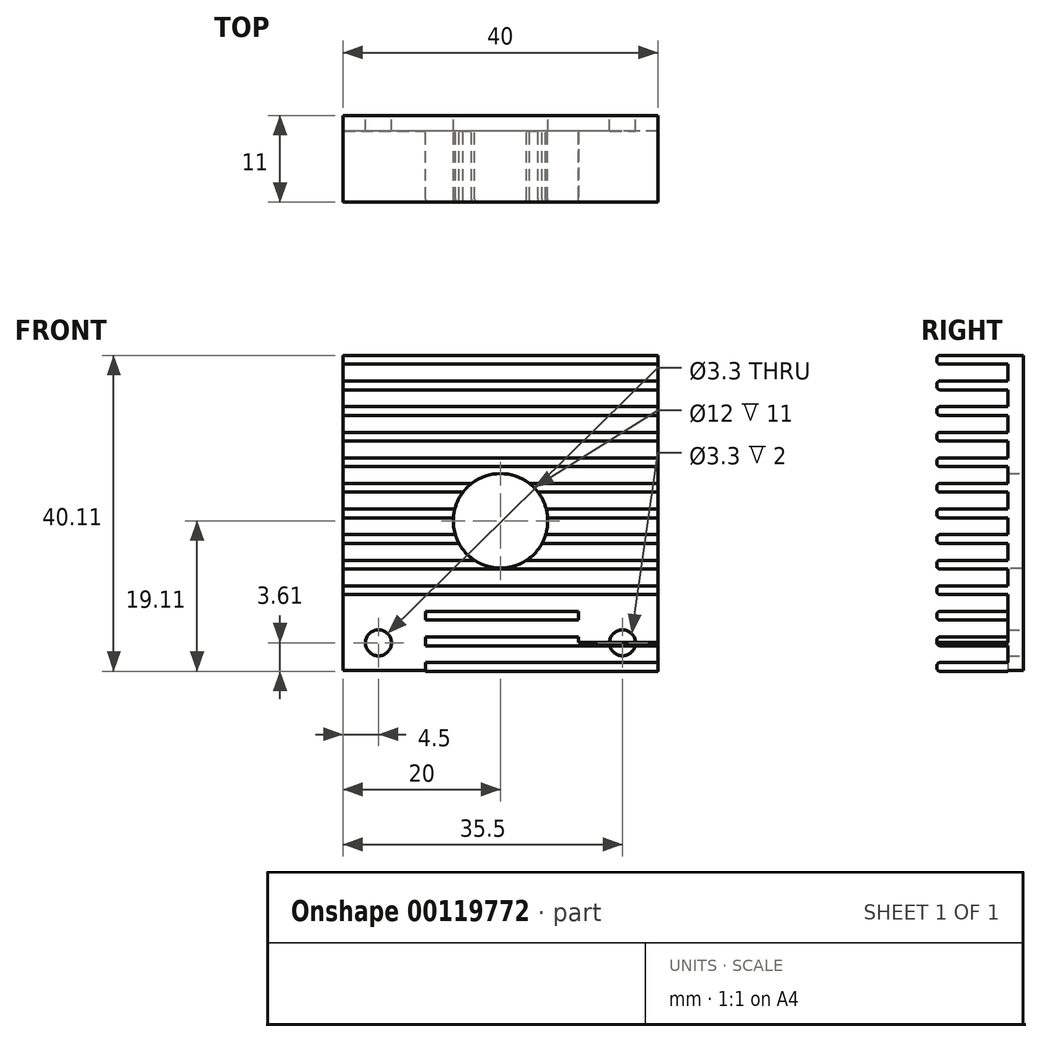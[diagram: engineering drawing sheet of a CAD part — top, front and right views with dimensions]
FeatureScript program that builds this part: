
annotation { "Feature Type Name" : "Feature", "Feature Type Description" : "" }
export const myFeature = defineFeature(function(context is Context, id is Id, definition is map)
    precondition{}
    {
        {
            var Q0;
            Q0=qCreatedBy(makeId("Top.planeOp"),FACE);
            var sketch = newSketch(context, id + "F0", { "sketchPlane" : qUnion([Q0])});
            skLineSegment(sketch, "E0", {"start": v(0, 20) * mm, "end": v(0, -20) * mm, "construction": true});
            skLineSegment(sketch, "E1", {"start": v(20, 20) * mm, "end": v(20, -20) * mm});
            skLineSegment(sketch, "E2", {"start": v(-20, 20) * mm, "end": v(-20, -20) * mm});
            skLineSegment(sketch, "E3", {"start": v(-20, 0) * mm, "end": v(20, 0) * mm, "construction": true});
            skLineSegment(sketch, "E4", {"start": v(-20, 20) * mm, "end": v(20, 20) * mm});
            skLineSegment(sketch, "E5", {"start": v(-20, -20) * mm, "end": v(20, -20) * mm});
            skPoint(sketch, "E6.orphan", {"position": v(-43.73, 20) * mm});
            skPoint(sketch, "E7.orphan", {"position": v(-42.9, 0) * mm});
            skPoint(sketch, "E8.orphan", {"position": v(-42.07, -20) * mm});
            skPoint(sketch, "E9.orphan", {"position": v(20, 28.35) * mm});
            skPoint(sketch, "E10.orphan", {"position": v(0, 28.12) * mm});
            skPoint(sketch, "E11.orphan", {"position": v(-20, 28.93) * mm});
            skLineSegment(sketch, "E12", {"start": v(-26.22, -16.5) * mm, "end": v(31.97, -16.5) * mm, "construction": true});
            skLineSegment(sketch, "E13", {"start": v(15.5, -23.6) * mm, "end": v(15.5, 22.14) * mm, "construction": true});
            skLineSegment(sketch, "E14", {"start": v(-15.5, 22.27) * mm, "end": v(-15.5, -32.23) * mm, "construction": true});
            skCircle(sketch, "E15", {"center": v(-15.5, -16.5) * mm, "radius": 1.65 * mm});
            skCircle(sketch, "E16", {"center": v(15.5, -16.5) * mm, "radius": 1.65 * mm});
            skLineSegment(sketch, "E17", {"start": v(9.9, 22.51) * mm, "end": v(9.9, -37.4) * mm, "construction": true});
            skLineSegment(sketch, "E18", {"start": v(-9.5, 22.14) * mm, "end": v(-9.5, -26.68) * mm, "construction": true});
            skLineSegment(sketch, "E19", {"start": v(-28.44, -10.5) * mm, "end": v(54.9, -10.5) * mm, "construction": true});
            skLineSegment(sketch, "E20", {"start": v(9.9, -10.5) * mm, "end": v(9.9, -20) * mm});
            skLineSegment(sketch, "E21", {"start": v(9.9, -10.5) * mm, "end": v(20, -10.5) * mm});
            skLineSegment(sketch, "E22", {"start": v(-20, -10.5) * mm, "end": v(-9.5, -10.5) * mm});
            skLineSegment(sketch, "E23", {"start": v(-9.5, -10.5) * mm, "end": v(-9.5, -20) * mm});
            skPoint(sketch, "E24", {"position": v(0, -1) * mm});
            skCircle(sketch, "E25", {"center": v(0, -1) * mm, "radius": 6 * mm});
            skSolve(sketch);
        }
        {
            var Q0;
            {var subQ4=sQuery(id+"F0.wireOp",EDGE,"E4");Q0=makeQuery(id+"F0.imprint","IMPRINT",FACE,{"disambiguationData":[TD([[makeQuery(id+"F0.imprint","IMPRINT",EDGE,{"derivedFrom":subQ4}),-1.0]])]});}
            var Q1;
            Q1=makeQuery(id+"F0.imprint","IMPRINT",FACE,{"disambiguationData":[TD([[makeQuery(id+"F0.imprint","IMPRINT",EDGE,{"derivedFrom":sQuery(id+"F0.wireOp",EDGE,"E15")}),-1.0]])]});
            var Q2;
            Q2=makeQuery(id+"F0.imprint","IMPRINT",FACE,{"disambiguationData":[TD([[makeQuery(id+"F0.imprint","IMPRINT",EDGE,{"derivedFrom":sQuery(id+"F0.wireOp",EDGE,"E16")}),-1.0]])]});
            extrude(context, id + "F1", {"entities" : qUnion([Q0, Q1, Q2]), "depth" : 2 * mm, "offsetDistance" : 25 * mm});
        }
        {
            var Q0;
            Q0=qCreatedBy(makeId("Right.planeOp"),FACE);
            var sketch = newSketch(context, id + "F2", { "sketchPlane" : qUnion([Q0])});
            skLineSegment(sketch, "E26.0", {"start": v(20, 2) * mm, "end": v(-20, 2) * mm});
            skLineSegment(sketch, "E26.1", {"start": v(20, 2) * mm, "end": v(20, 0) * mm});
            skLineSegment(sketch, "E26.2", {"start": v(-20, 2) * mm, "end": v(-20, 0) * mm});
            skLineSegment(sketch, "E27", {"start": v(20, 2) * mm, "end": v(20, 11) * mm});
            skLineSegment(sketch, "E28", {"start": v(20, 11) * mm, "end": v(18.9, 11) * mm});
            skLineSegment(sketch, "E29", {"start": v(18.9, 11) * mm, "end": v(18.9, 2) * mm});
            skLineSegment(sketch, "E30", {"start": v(20, 2) * mm, "end": v(18.9, 2) * mm});
            skLineSegment(sketch, "E31.1.0.0", {"start": v(16.75, 2) * mm, "end": v(16.75, 11) * mm});
            skLineSegment(sketch, "E31.1.0.1", {"start": v(16.75, 11) * mm, "end": v(15.65, 11) * mm});
            skLineSegment(sketch, "E31.1.0.2", {"start": v(15.65, 11) * mm, "end": v(15.65, 2) * mm});
            skLineSegment(sketch, "E31.1.0.3", {"start": v(16.75, 2) * mm, "end": v(15.65, 2) * mm});
            skLineSegment(sketch, "E31.2.0.0", {"start": v(13.5, 2) * mm, "end": v(13.5, 11) * mm});
            skLineSegment(sketch, "E31.2.0.1", {"start": v(13.5, 11) * mm, "end": v(12.4, 11) * mm});
            skLineSegment(sketch, "E31.2.0.2", {"start": v(12.4, 11) * mm, "end": v(12.4, 2) * mm});
            skLineSegment(sketch, "E31.2.0.3", {"start": v(13.5, 2) * mm, "end": v(12.4, 2) * mm});
            skLineSegment(sketch, "E31.3.0.0", {"start": v(10.25, 2) * mm, "end": v(10.25, 11) * mm});
            skLineSegment(sketch, "E31.3.0.1", {"start": v(10.25, 11) * mm, "end": v(9.15, 11) * mm});
            skLineSegment(sketch, "E31.3.0.2", {"start": v(9.15, 11) * mm, "end": v(9.15, 2) * mm});
            skLineSegment(sketch, "E31.3.0.3", {"start": v(10.25, 2) * mm, "end": v(9.15, 2) * mm});
            skLineSegment(sketch, "E31.4.0.0", {"start": v(7, 2) * mm, "end": v(7, 11) * mm});
            skLineSegment(sketch, "E31.4.0.1", {"start": v(7, 11) * mm, "end": v(5.9, 11) * mm});
            skLineSegment(sketch, "E31.4.0.2", {"start": v(5.9, 11) * mm, "end": v(5.9, 2) * mm});
            skLineSegment(sketch, "E31.4.0.3", {"start": v(7, 2) * mm, "end": v(5.9, 2) * mm});
            skLineSegment(sketch, "E31.5.0.0", {"start": v(3.74, 2) * mm, "end": v(3.74, 11) * mm});
            skLineSegment(sketch, "E31.5.0.1", {"start": v(3.74, 11) * mm, "end": v(2.64, 11) * mm});
            skLineSegment(sketch, "E31.5.0.2", {"start": v(2.64, 11) * mm, "end": v(2.64, 2) * mm});
            skLineSegment(sketch, "E31.5.0.3", {"start": v(3.74, 2) * mm, "end": v(2.64, 2) * mm});
            skLineSegment(sketch, "E31.6.0.0", {"start": v(0.5, 2) * mm, "end": v(0.5, 11) * mm});
            skLineSegment(sketch, "E31.6.0.1", {"start": v(0.5, 11) * mm, "end": v(-0.6, 11) * mm});
            skLineSegment(sketch, "E31.6.0.2", {"start": v(-0.6, 11) * mm, "end": v(-0.6, 2) * mm});
            skLineSegment(sketch, "E31.6.0.3", {"start": v(0.5, 2) * mm, "end": v(-0.6, 2) * mm});
            skLineSegment(sketch, "E31.7.0.0", {"start": v(-2.76, 2) * mm, "end": v(-2.76, 11) * mm});
            skLineSegment(sketch, "E31.7.0.1", {"start": v(-2.76, 11) * mm, "end": v(-3.86, 11) * mm});
            skLineSegment(sketch, "E31.7.0.2", {"start": v(-3.86, 11) * mm, "end": v(-3.86, 2) * mm});
            skLineSegment(sketch, "E31.7.0.3", {"start": v(-2.76, 2) * mm, "end": v(-3.86, 2) * mm});
            skLineSegment(sketch, "E31.8.0.0", {"start": v(-6, 2) * mm, "end": v(-6, 11) * mm});
            skLineSegment(sketch, "E31.8.0.1", {"start": v(-6, 11) * mm, "end": v(-7.1, 11) * mm});
            skLineSegment(sketch, "E31.8.0.2", {"start": v(-7.1, 11) * mm, "end": v(-7.1, 2) * mm});
            skLineSegment(sketch, "E31.8.0.3", {"start": v(-6, 2) * mm, "end": v(-7.1, 2) * mm});
            skLineSegment(sketch, "E31.9.0.0", {"start": v(-9.26, 2) * mm, "end": v(-9.26, 11) * mm});
            skLineSegment(sketch, "E31.9.0.1", {"start": v(-9.26, 11) * mm, "end": v(-10.36, 11) * mm});
            skLineSegment(sketch, "E31.9.0.2", {"start": v(-10.36, 11) * mm, "end": v(-10.36, 2) * mm});
            skLineSegment(sketch, "E31.9.0.3", {"start": v(-9.26, 2) * mm, "end": v(-10.36, 2) * mm});
            skLineSegment(sketch, "E31.10.0.0", {"start": v(-12.51, 2) * mm, "end": v(-12.51, 11) * mm});
            skLineSegment(sketch, "E31.10.0.1", {"start": v(-12.51, 11) * mm, "end": v(-13.61, 11) * mm});
            skLineSegment(sketch, "E31.10.0.2", {"start": v(-13.61, 11) * mm, "end": v(-13.61, 2) * mm});
            skLineSegment(sketch, "E31.10.0.3", {"start": v(-12.51, 2) * mm, "end": v(-13.61, 2) * mm});
            skLineSegment(sketch, "E31.11.0.0", {"start": v(-15.76, 2) * mm, "end": v(-15.76, 11) * mm});
            skLineSegment(sketch, "E31.11.0.1", {"start": v(-15.76, 11) * mm, "end": v(-16.86, 11) * mm});
            skLineSegment(sketch, "E31.11.0.2", {"start": v(-16.86, 11) * mm, "end": v(-16.86, 2) * mm});
            skLineSegment(sketch, "E31.11.0.3", {"start": v(-15.76, 2) * mm, "end": v(-16.86, 2) * mm});
            skLineSegment(sketch, "E31.12.0.0", {"start": v(-19.01, 2) * mm, "end": v(-19.01, 11) * mm});
            skLineSegment(sketch, "E31.12.0.1", {"start": v(-19.01, 11) * mm, "end": v(-20.11, 11) * mm});
            skLineSegment(sketch, "E31.12.0.2", {"start": v(-20.11, 11) * mm, "end": v(-20.11, 2) * mm});
            skLineSegment(sketch, "E31.12.0.3", {"start": v(-19.01, 2) * mm, "end": v(-20.11, 2) * mm});
            skLineSegment(sketch, "E31.direction1", {"start": v(20, 2) * mm, "end": v(16.75, 2) * mm, "construction": true});
            skSolve(sketch);
        }
        {
            var Q0;
            Q0=makeQuery(id+"F2.imprint","IMPRINT",FACE,{"disambiguationData":[TD([[makeQuery(id+"F2.imprint","IMPRINT",EDGE,{"derivedFrom":sQuery(id+"F2.wireOp",EDGE,"E27")}),1.0]])]});
            var Q1;
            Q1=makeQuery(id+"F2.imprint","IMPRINT",FACE,{"disambiguationData":[TD([[makeQuery(id+"F2.imprint","IMPRINT",EDGE,{"derivedFrom":sQuery(id+"F2.wireOp",EDGE,"E31.1.0.0")}),1.0]])]});
            var Q2;
            Q2=makeQuery(id+"F2.imprint","IMPRINT",FACE,{"disambiguationData":[TD([[makeQuery(id+"F2.imprint","IMPRINT",EDGE,{"derivedFrom":sQuery(id+"F2.wireOp",EDGE,"E31.2.0.0")}),1.0]])]});
            var Q3;
            Q3=makeQuery(id+"F2.imprint","IMPRINT",FACE,{"disambiguationData":[TD([[makeQuery(id+"F2.imprint","IMPRINT",EDGE,{"derivedFrom":sQuery(id+"F2.wireOp",EDGE,"E31.3.0.0")}),1.0]])]});
            var Q4;
            Q4=makeQuery(id+"F2.imprint","IMPRINT",FACE,{"disambiguationData":[TD([[makeQuery(id+"F2.imprint","IMPRINT",EDGE,{"derivedFrom":sQuery(id+"F2.wireOp",EDGE,"E31.4.0.0")}),1.0]])]});
            var Q5;
            Q5=makeQuery(id+"F2.imprint","IMPRINT",FACE,{"disambiguationData":[TD([[makeQuery(id+"F2.imprint","IMPRINT",EDGE,{"derivedFrom":sQuery(id+"F2.wireOp",EDGE,"E31.5.0.0")}),1.0]])]});
            var Q6;
            Q6=makeQuery(id+"F2.imprint","IMPRINT",FACE,{"disambiguationData":[TD([[makeQuery(id+"F2.imprint","IMPRINT",EDGE,{"derivedFrom":sQuery(id+"F2.wireOp",EDGE,"E31.6.0.0")}),1.0]])]});
            var Q7;
            Q7=makeQuery(id+"F2.imprint","IMPRINT",FACE,{"disambiguationData":[TD([[makeQuery(id+"F2.imprint","IMPRINT",EDGE,{"derivedFrom":sQuery(id+"F2.wireOp",EDGE,"E31.7.0.0")}),1.0]])]});
            var Q8;
            Q8=makeQuery(id+"F2.imprint","IMPRINT",FACE,{"disambiguationData":[TD([[makeQuery(id+"F2.imprint","IMPRINT",EDGE,{"derivedFrom":sQuery(id+"F2.wireOp",EDGE,"E31.9.0.0")}),1.0]])]});
            var Q9;
            Q9=makeQuery(id+"F2.imprint","IMPRINT",FACE,{"disambiguationData":[TD([[makeQuery(id+"F2.imprint","IMPRINT",EDGE,{"derivedFrom":sQuery(id+"F2.wireOp",EDGE,"E31.10.0.0")}),1.0]])]});
            var Q10;
            Q10=makeQuery(id+"F2.imprint","IMPRINT",FACE,{"disambiguationData":[TD([[makeQuery(id+"F2.imprint","IMPRINT",EDGE,{"derivedFrom":sQuery(id+"F2.wireOp",EDGE,"E31.11.0.0")}),1.0]])]});
            var Q11;
            Q11=makeQuery(id+"F2.imprint","IMPRINT",FACE,{"disambiguationData":[TD([[makeQuery(id+"F2.imprint","IMPRINT",EDGE,{"derivedFrom":sQuery(id+"F2.wireOp",EDGE,"E31.12.0.0")}),1.0]])]});
            var Q12;
            Q12=makeQuery(id+"F2.imprint","IMPRINT",FACE,{"disambiguationData":[TD([[makeQuery(id+"F2.imprint","IMPRINT",EDGE,{"derivedFrom":sQuery(id+"F2.wireOp",EDGE,"E31.8.0.0")}),1.0]])]});
            extrude(context, id + "F3", {"entities" : qUnion([Q0, Q1, Q2, Q3, Q4, Q5, Q6, Q7, Q8, Q9, Q10, Q11, Q12]), "operationType" : NewBodyOperationType.ADD, "depth" : 40 * mm, "offsetDistance" : 25 * mm, "symmetric" : true});
        }
        {
            var Q0;
            Q0=makeQuery(id+"F0.imprint","IMPRINT",FACE,{"disambiguationData":[TD([[makeQuery(id+"F0.imprint","IMPRINT",EDGE,{"derivedFrom":sQuery(id+"F0.wireOp",EDGE,"E25")}),1.0]])]});
            extrude(context, id + "F4", {"entities" : qUnion([Q0]), "operationType" : NewBodyOperationType.REMOVE, "depth" : 19 * mm, "offsetDistance" : 25 * mm});
        }
        {
            var Q0;
            Q0=makeQuery(id+"F3.opExtrude","SWEPT_EDGE",EDGE,{"disambiguationData":[OSD([sQuery(id+"F2.wireOp",EDGE,"E27"),sQuery(id+"F2.wireOp",EDGE,"E28")])]});
            var Q1;
            Q1=makeQuery(id+"F3.opExtrude","SWEPT_EDGE",EDGE,{"disambiguationData":[OSD([sQuery(id+"F2.wireOp",EDGE,"E28"),sQuery(id+"F2.wireOp",EDGE,"E29")])]});
            var Q2;
            Q2=makeQuery(id+"F3.opExtrude","SWEPT_EDGE",EDGE,{"disambiguationData":[OSD([sQuery(id+"F2.wireOp",EDGE,"E31.1.0.0"),sQuery(id+"F2.wireOp",EDGE,"E31.1.0.1")])]});
            var Q3;
            Q3=makeQuery(id+"F3.opExtrude","SWEPT_EDGE",EDGE,{"disambiguationData":[OSD([sQuery(id+"F2.wireOp",EDGE,"E31.1.0.1"),sQuery(id+"F2.wireOp",EDGE,"E31.1.0.2")])]});
            var Q4;
            Q4=makeQuery(id+"F3.opExtrude","SWEPT_EDGE",EDGE,{"disambiguationData":[OSD([sQuery(id+"F2.wireOp",EDGE,"E31.2.0.0"),sQuery(id+"F2.wireOp",EDGE,"E31.2.0.1")])]});
            var Q5;
            Q5=makeQuery(id+"F3.opExtrude","SWEPT_EDGE",EDGE,{"disambiguationData":[OSD([sQuery(id+"F2.wireOp",EDGE,"E31.2.0.1"),sQuery(id+"F2.wireOp",EDGE,"E31.2.0.2")])]});
            var Q6;
            Q6=makeQuery(id+"F3.opExtrude","SWEPT_EDGE",EDGE,{"disambiguationData":[OSD([sQuery(id+"F2.wireOp",EDGE,"E31.3.0.0"),sQuery(id+"F2.wireOp",EDGE,"E31.3.0.1")])]});
            var Q7;
            Q7=makeQuery(id+"F3.opExtrude","SWEPT_EDGE",EDGE,{"disambiguationData":[OSD([sQuery(id+"F2.wireOp",EDGE,"E31.3.0.1"),sQuery(id+"F2.wireOp",EDGE,"E31.3.0.2")])]});
            var Q8;
            Q8=makeQuery(id+"F3.opExtrude","SWEPT_EDGE",EDGE,{"disambiguationData":[OSD([sQuery(id+"F2.wireOp",EDGE,"E31.4.0.0"),sQuery(id+"F2.wireOp",EDGE,"E31.4.0.1")])]});
            var Q9;
            Q9=makeQuery(id+"F3.opExtrude","SWEPT_EDGE",EDGE,{"disambiguationData":[OSD([sQuery(id+"F2.wireOp",EDGE,"E31.4.0.1"),sQuery(id+"F2.wireOp",EDGE,"E31.4.0.2")])]});
            var Q10;
            Q10=makeQuery(id+"F3.opExtrude","SWEPT_EDGE",EDGE,{"disambiguationData":[OSD([sQuery(id+"F2.wireOp",EDGE,"E31.5.0.0"),sQuery(id+"F2.wireOp",EDGE,"E31.5.0.1")])]});
            var Q11;
            Q11=makeQuery(id+"F3.opExtrude","SWEPT_EDGE",EDGE,{"disambiguationData":[OSD([sQuery(id+"F2.wireOp",EDGE,"E31.5.0.1"),sQuery(id+"F2.wireOp",EDGE,"E31.5.0.2")])]});
            var Q12;
            Q12=makeQuery(id+"F3.opExtrude","SWEPT_EDGE",EDGE,{"disambiguationData":[OSD([sQuery(id+"F2.wireOp",EDGE,"E31.6.0.0"),sQuery(id+"F2.wireOp",EDGE,"E31.6.0.1")])]});
            var Q13;
            Q13=makeQuery(id+"F3.opExtrude","SWEPT_EDGE",EDGE,{"disambiguationData":[OSD([sQuery(id+"F2.wireOp",EDGE,"E31.6.0.1"),sQuery(id+"F2.wireOp",EDGE,"E31.6.0.2")])]});
            var Q14;
            Q14=makeQuery(id+"F3.opExtrude","SWEPT_EDGE",EDGE,{"disambiguationData":[OSD([sQuery(id+"F2.wireOp",EDGE,"E31.7.0.0"),sQuery(id+"F2.wireOp",EDGE,"E31.7.0.1")])]});
            var Q15;
            Q15=makeQuery(id+"F3.opExtrude","SWEPT_EDGE",EDGE,{"disambiguationData":[OSD([sQuery(id+"F2.wireOp",EDGE,"E31.7.0.1"),sQuery(id+"F2.wireOp",EDGE,"E31.7.0.2")])]});
            var Q16;
            Q16=makeQuery(id+"F3.opExtrude","SWEPT_EDGE",EDGE,{"disambiguationData":[OSD([sQuery(id+"F2.wireOp",EDGE,"E31.8.0.0"),sQuery(id+"F2.wireOp",EDGE,"E31.8.0.1")])]});
            var Q17;
            Q17=makeQuery(id+"F3.opExtrude","SWEPT_EDGE",EDGE,{"disambiguationData":[OSD([sQuery(id+"F2.wireOp",EDGE,"E31.8.0.1"),sQuery(id+"F2.wireOp",EDGE,"E31.8.0.2")])]});
            var Q18;
            Q18=makeQuery(id+"F3.opExtrude","SWEPT_EDGE",EDGE,{"disambiguationData":[OSD([sQuery(id+"F2.wireOp",EDGE,"E31.9.0.0"),sQuery(id+"F2.wireOp",EDGE,"E31.9.0.1")])]});
            var Q19;
            Q19=makeQuery(id+"F3.opExtrude","SWEPT_EDGE",EDGE,{"disambiguationData":[OSD([sQuery(id+"F2.wireOp",EDGE,"E31.9.0.1"),sQuery(id+"F2.wireOp",EDGE,"E31.9.0.2")])]});
            var Q20;
            Q20=makeQuery(id+"F4.opExtrude","SWEPT_EDGE",EDGE,{"disambiguationData":[OSD([sQuery(id+"F2.wireOp",EDGE,"E31.10.0.0"),sQuery(id+"F2.wireOp",EDGE,"E31.10.0.1")])]});
            var Q21;
            Q21=makeQuery(id+"F4.opExtrude","SWEPT_EDGE",EDGE,{"disambiguationData":[OSD([sQuery(id+"F2.wireOp",EDGE,"E31.10.0.1"),sQuery(id+"F2.wireOp",EDGE,"E31.10.0.2")])]});
            var Q22;
            Q22=makeQuery(id+"F4.opExtrude","SWEPT_EDGE",EDGE,{"disambiguationData":[OSD([sQuery(id+"F2.wireOp",EDGE,"E31.11.0.0"),sQuery(id+"F2.wireOp",EDGE,"E31.11.0.1")])]});
            var Q23;
            Q23=makeQuery(id+"F4.opExtrude","SWEPT_EDGE",EDGE,{"disambiguationData":[OSD([sQuery(id+"F2.wireOp",EDGE,"E31.11.0.1"),sQuery(id+"F2.wireOp",EDGE,"E31.11.0.2")])]});
            var Q24;
            Q24=makeQuery(id+"F4.opExtrude","SWEPT_EDGE",EDGE,{"disambiguationData":[OSD([sQuery(id+"F2.wireOp",EDGE,"E31.12.0.0"),sQuery(id+"F2.wireOp",EDGE,"E31.12.0.1")])]});
            var Q25;
            Q25=makeQuery(id+"F4.opExtrude","SWEPT_EDGE",EDGE,{"disambiguationData":[OSD([sQuery(id+"F2.wireOp",EDGE,"E31.12.0.1"),sQuery(id+"F2.wireOp",EDGE,"E31.12.0.2")])]});
            var Q26;
            Q26=makeQuery(id+"F3.opExtrude","SWEPT_EDGE",EDGE,{"disambiguationData":[OSD([sQuery(id+"F2.wireOp",EDGE,"E31.10.0.1"),sQuery(id+"F2.wireOp",EDGE,"E31.10.0.2")])]});
            var Q27;
            Q27=makeQuery(id+"F3.opExtrude","SWEPT_EDGE",EDGE,{"disambiguationData":[OSD([sQuery(id+"F2.wireOp",EDGE,"E31.10.0.0"),sQuery(id+"F2.wireOp",EDGE,"E31.10.0.1")])]});
            var Q28;
            Q28=makeQuery(id+"F3.opExtrude","SWEPT_EDGE",EDGE,{"disambiguationData":[OSD([sQuery(id+"F2.wireOp",EDGE,"E31.11.0.1"),sQuery(id+"F2.wireOp",EDGE,"E31.11.0.2")])]});
            var Q29;
            Q29=makeQuery(id+"F3.opExtrude","SWEPT_EDGE",EDGE,{"disambiguationData":[OSD([sQuery(id+"F2.wireOp",EDGE,"E31.11.0.0"),sQuery(id+"F2.wireOp",EDGE,"E31.11.0.1")])]});
            var Q30;
            Q30=makeQuery(id+"F3.opExtrude","SWEPT_EDGE",EDGE,{"disambiguationData":[OSD([sQuery(id+"F2.wireOp",EDGE,"E31.12.0.0"),sQuery(id+"F2.wireOp",EDGE,"E31.12.0.1")])]});
            var Q31;
            Q31=makeQuery(id+"F3.opExtrude","SWEPT_EDGE",EDGE,{"disambiguationData":[OSD([sQuery(id+"F2.wireOp",EDGE,"E31.12.0.1"),sQuery(id+"F2.wireOp",EDGE,"E31.12.0.2")])]});
            fillet(context, id + "F5", {"entities" : qUnion([Q0, Q1, Q2, Q3, Q4, Q5, Q6, Q7, Q8, Q9, Q10, Q11, Q12, Q13, Q14, Q15, Q16, Q17, Q18, Q19, Q20, Q21, Q22, Q23, Q24, Q25, Q26, Q27, Q28, Q29, Q30, Q31]), "radius" : 0.4 * mm, "tangentPropagation" : true, "allowEdgeOverflow" : false});
        }
        {
            var Q0;
            Q0=makeQuery(id+"F3.opExtrude","SWEPT_FACE",FACE,{"disambiguationData":[OSD([sQuery(id+"F2.wireOp",EDGE,"E31.11.0.1")])]});
            var sketch = newSketch(context, id + "F6", { "sketchPlane" : qUnion([Q0])});
            skLineSegment(sketch, "E32.0", {"start": v(-9.5, -10.5) * mm, "end": v(-9.5, -20) * mm});
            skLineSegment(sketch, "E32.1", {"start": v(-20, -10.5) * mm, "end": v(-9.5, -10.5) * mm});
            skLineSegment(sketch, "E32.2", {"start": v(9.9, -10.5) * mm, "end": v(9.9, -20) * mm});
            skLineSegment(sketch, "E32.3", {"start": v(9.9, -10.5) * mm, "end": v(20, -10.5) * mm});
            skLineSegment(sketch, "E33", {"start": v(-20, -10.5) * mm, "end": v(-20, -20) * mm});
            skLineSegment(sketch, "E34", {"start": v(-20, -20) * mm, "end": v(-9.5, -20) * mm});
            skLineSegment(sketch, "E35", {"start": v(20, -10.5) * mm, "end": v(20, -20) * mm});
            skLineSegment(sketch, "E36", {"start": v(20, -20) * mm, "end": v(9.9, -20) * mm});
            skLineSegment(sketch, "E37.trimOffspring", {"start": v(9.9, -20) * mm, "end": v(20, -20) * mm});
            skPoint(sketch, "E38.orphan", {"position": v(-20, 20) * mm});
            skLineSegment(sketch, "E39", {"start": v(-9.5, -20) * mm, "end": v(-9.5, -21.12) * mm});
            skLineSegment(sketch, "E40", {"start": v(-9.5, -21.12) * mm, "end": v(-20, -21.12) * mm});
            skLineSegment(sketch, "E41", {"start": v(-20, -21.12) * mm, "end": v(-20, -20) * mm});
            skLineSegment(sketch, "E42", {"start": v(9.9, -20) * mm, "end": v(9.9, -21.12) * mm});
            skLineSegment(sketch, "E43", {"start": v(9.9, -21.12) * mm, "end": v(20, -21.12) * mm});
            skLineSegment(sketch, "E44", {"start": v(20, -21.12) * mm, "end": v(20, -20) * mm});
            skSolve(sketch);
        }
        {
            var Q0;
            {var subQ0=sQuery(id+"F6.wireOp",EDGE,"E32.1");Q0=makeQuery(id+"F6.imprint","IMPRINT",FACE,{"disambiguationData":[TD([[makeQuery(id+"F6.imprint","IMPRINT",EDGE,{"derivedFrom":subQ0}),-1.0]])]});}
            var Q1;
            {var subQ0=sQuery(id+"F6.wireOp",EDGE,"E34");Q1=makeQuery(id+"F6.imprint","IMPRINT",FACE,{"disambiguationData":[TD([[makeQuery(id+"F6.imprint","IMPRINT",EDGE,{"derivedFrom":subQ0}),1.0]])]});}
            var Q2;
            {var subQ0=sQuery(id+"F6.wireOp",EDGE,"E32.0");var subQ1=sQuery(id+"F2.wireOp",EDGE,"E31.11.0.1");var subQ2=makeQuery(id+"F3.opExtrude","SWEPT_FACE",FACE,{"disambiguationData":[OSD([subQ1])]});var subQ3=makeQuery(id+"F5.opFillet","BLEND_EDGE",EDGE,{"blendedFrom":[makeQuery(id+"F3.opExtrude","SWEPT_EDGE",EDGE,{"disambiguationData":[OSD([sQuery(id+"F2.wireOp",EDGE,"E31.11.0.0"),subQ1])]}),subQ2],"blendedInto":[subQ2]});var subQ4=makeQuery(id+"F6.imprint","INTERSECT",VERTEX,{"derivedFrom":[subQ3,subQ0]});Q2=makeQuery(id+"F6.imprint","IMPRINT",FACE,{"disambiguationData":[TD([[makeQuery(id+"F6.imprint","IMPRINT",EDGE,{"disambiguationData":[TD([[subQ4,-1.0]])],"derivedFrom":subQ0}),-1.0]])]});}
            var Q3;
            {var subQ0=sQuery(id+"F6.wireOp",EDGE,"E32.3");Q3=makeQuery(id+"F6.imprint","IMPRINT",FACE,{"disambiguationData":[TD([[makeQuery(id+"F6.imprint","IMPRINT",EDGE,{"derivedFrom":subQ0}),-1.0]])]});}
            var Q4;
            {var subQ0=sQuery(id+"F6.wireOp",EDGE,"E32.2");var subQ1=sQuery(id+"F2.wireOp",EDGE,"E31.11.0.1");var subQ2=makeQuery(id+"F3.opExtrude","SWEPT_FACE",FACE,{"disambiguationData":[OSD([subQ1])]});var subQ3=makeQuery(id+"F5.opFillet","BLEND_EDGE",EDGE,{"blendedFrom":[makeQuery(id+"F3.opExtrude","SWEPT_EDGE",EDGE,{"disambiguationData":[OSD([sQuery(id+"F2.wireOp",EDGE,"E31.11.0.0"),subQ1])]}),subQ2],"blendedInto":[subQ2]});var subQ4=makeQuery(id+"F6.imprint","INTERSECT",VERTEX,{"derivedFrom":[subQ3,subQ0]});Q4=makeQuery(id+"F6.imprint","IMPRINT",FACE,{"disambiguationData":[TD([[makeQuery(id+"F6.imprint","IMPRINT",EDGE,{"disambiguationData":[TD([[subQ4,-1.0]])],"derivedFrom":subQ0}),1.0]])]});}
            var Q5;
            {var subQ0=sQuery(id+"F6.wireOp",EDGE,"E37.trimOffspring");Q5=makeQuery(id+"F6.imprint","IMPRINT",FACE,{"disambiguationData":[TD([[makeQuery(id+"F6.imprint","IMPRINT",EDGE,{"derivedFrom":subQ0}),1.0]])]});}
            var Q6;
            Q6=makeQuery(id+"F6.imprint","IMPRINT",FACE,{"disambiguationData":[TD([[makeQuery(id+"F6.imprint","IMPRINT",EDGE,{"derivedFrom":sQuery(id+"F6.wireOp",EDGE,"E34")}),-1.0]])]});
            var Q7;
            Q7=makeQuery(id+"F6.imprint","IMPRINT",FACE,{"disambiguationData":[TD([[makeQuery(id+"F6.imprint","IMPRINT",EDGE,{"derivedFrom":sQuery(id+"F6.wireOp",EDGE,"E37.trimOffspring")}),-1.0]])]});
            extrude(context, id + "F7", {"entities" : qUnion([Q0, Q1, Q2, Q3, Q4, Q5, Q6, Q7]), "operationType" : NewBodyOperationType.REMOVE, "oppositeDirection" : true, "depth" : 9 * mm, "offsetDistance" : 25 * mm});
        }
        {
            var Q0;
            Q0=makeQuery(id+"F1.opExtrude","SWEPT_BODY",BODY,{"disambiguationData":[OSD([sQuery(id+"F0.wireOp",EDGE,"E1"),sQuery(id+"F0.wireOp",EDGE,"E2"),sQuery(id+"F0.wireOp",EDGE,"E4"),sQuery(id+"F0.wireOp",EDGE,"E5"),sQuery(id+"F0.wireOp",EDGE,"l9XOs5mF-tHXF-YdOa-aCKa-W7GI6oJj2D0n"),sQuery(id+"F0.wireOp",EDGE,"E15"),sQuery(id+"F0.wireOp",EDGE,"E16")])]});
            var Q1;
            Q1=makeQuery(id+"F1.opExtrude","CAP_EDGE",EDGE,{"disambiguationData":[OSD([sQuery(id+"F0.wireOp",EDGE,"E5")])],"isStart":true});
            transform(context, id + "F8", {"entities" : qUnion([Q0]), "transformType" : TransformType.ROTATION, "transformAxis" : qUnion([Q1]), "angle" : 90 * degree, "makeCopy" : false});
        }
    });
